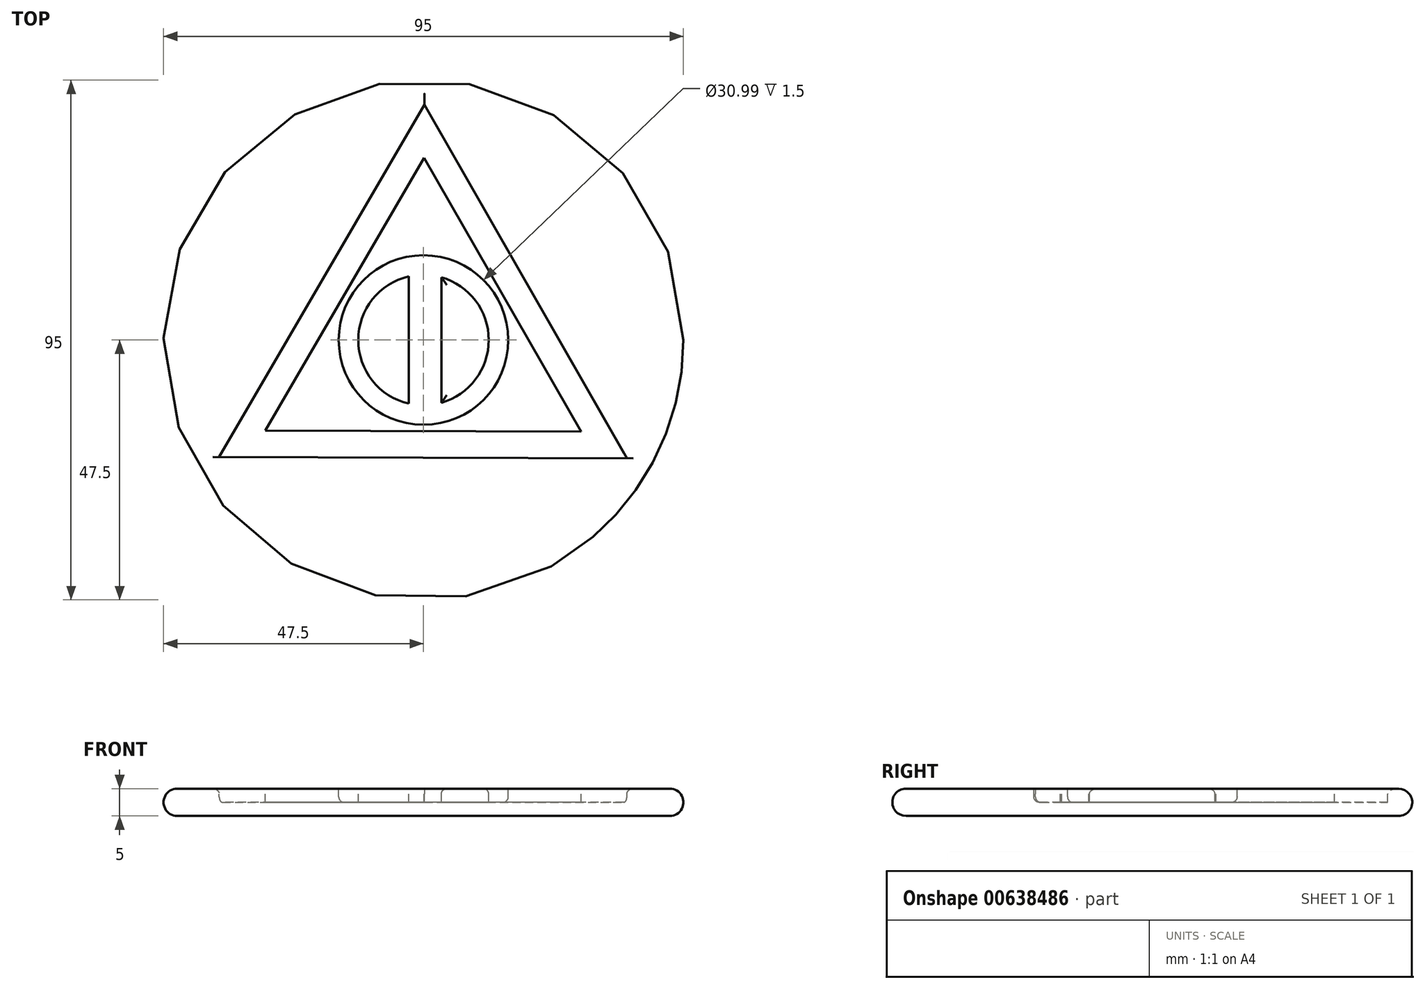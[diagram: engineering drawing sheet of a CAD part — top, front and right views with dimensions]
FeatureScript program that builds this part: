
annotation { "Feature Type Name" : "Feature", "Feature Type Description" : "" }
export const myFeature = defineFeature(function(context is Context, id is Id, definition is map)
    precondition{}
    {
        {
            var Q0;
            Q0=qCreatedBy(makeId("Top.planeOp"),FACE);
            var sketch = newSketch(context, id + "F0", { "sketchPlane" : qUnion([Q0])});
            skCircle(sketch, "E0", {"center": v(0, 0) * mm, "radius": 47.5 * mm});
            skSolve(sketch);
        }
        {
            var Q0;
            Q0=makeQuery(id+"F0.imprint","IMPRINT",FACE,{"disambiguationData":[TD([[makeQuery(id+"F0.imprint","IMPRINT",EDGE,{"derivedFrom":sQuery(id+"F0.wireOp",EDGE,"E0")}),1.0]])]});
            extrude(context, id + "F1", {"entities" : qUnion([Q0]), "depth" : 5 * mm, "offsetDistance" : 25.4 * mm});
        }
        {
            var Q0;
            Q0=makeQuery(id+"F1.opExtrude","CAP_FACE",FACE,{"disambiguationData":[OSD([sQuery(id+"F0.wireOp",EDGE,"E0")])],"isStart":false});
            var sketch = newSketch(context, id + "F2", { "sketchPlane" : qUnion([Q0])});
            skCircle(sketch, "E1.cCircle", {"center": v(0, 0) * mm, "radius": 21.5 * mm, "construction": true});
            skLineSegment(sketch, "E1.0", {"start": v(37.17, -21.65) * mm, "end": v(-37.34, -21.36) * mm});
            skLineSegment(sketch, "E1.1", {"start": v(-37.34, -21.36) * mm, "end": v(0.17, 43.01) * mm});
            skLineSegment(sketch, "E1.2", {"start": v(0.17, 43.01) * mm, "end": v(37.17, -21.65) * mm});
            skPoint(sketch, "E1.0.midPoint", {"position": v(-0.08, -21.5) * mm});
            skCircle(sketch, "E2.cCircle", {"center": v(0, 0) * mm, "radius": 16.66 * mm, "construction": true});
            skLineSegment(sketch, "E2.0", {"start": v(0.13, 33.32) * mm, "end": v(28.8, -16.77) * mm});
            skLineSegment(sketch, "E2.1", {"start": v(28.8, -16.77) * mm, "end": v(-28.92, -16.55) * mm});
            skLineSegment(sketch, "E2.2", {"start": v(-28.92, -16.55) * mm, "end": v(0.13, 33.32) * mm});
            skPoint(sketch, "E2.0.midPoint", {"position": v(14.46, 8.27) * mm});
            skSolve(sketch);
        }
        {
            var Q0;
            Q0 = qSketchRegion(id + "F2", true);
            extrude(context, id + "F3", {"entities" : qUnion([Q0]), "operationType" : NewBodyOperationType.REMOVE, "oppositeDirection" : true, "depth" : 2.5 * mm, "offsetDistance" : 25 * mm});
        }
        {
            var Q0;
            Q0=makeQuery(id+"F3.boolean.opBoolean","SPLIT",FACE,{"disambiguationData":[TD([makeQuery(id+"F3.opExtrude","SWEPT_FACE",FACE,{"disambiguationData":[OSD([sQuery(id+"F2.wireOp",EDGE,"E2.0")])]})])],"derivedFrom":makeQuery(id+"F1.opExtrude","CAP_FACE",FACE,{"disambiguationData":[OSD([sQuery(id+"F0.wireOp",EDGE,"E0")])],"isStart":false})});
            var sketch = newSketch(context, id + "F4", { "sketchPlane" : qUnion([Q0])});
            skCircle(sketch, "E3", {"center": v(0, 0) * mm, "radius": 15.5 * mm});
            skCircle(sketch, "E4", {"center": v(0, 0) * mm, "radius": 11.92 * mm});
            skSolve(sketch);
        }
        {
            var Q0;
            Q0=makeQuery(id+"F4.imprint","IMPRINT",FACE,{"disambiguationData":[TD([[makeQuery(id+"F4.imprint","IMPRINT",EDGE,{"derivedFrom":sQuery(id+"F4.wireOp",EDGE,"E3")}),1.0]])]});
            extrude(context, id + "F5", {"entities" : qUnion([Q0]), "operationType" : NewBodyOperationType.REMOVE, "oppositeDirection" : true, "depth" : 2.5 * mm, "offsetDistance" : 25 * mm});
        }
        {
            var Q0;
            {var subQ0=makeQuery(id+"F3.opExtrude","SWEPT_FACE",FACE,{"disambiguationData":[OSD([sQuery(id+"F2.wireOp",EDGE,"E2.0")])]});Q0=makeQuery(id+"F5.boolean.opBoolean","SPLIT",FACE,{"disambiguationData":[TD([makeQuery(id+"F3.boolean.opBoolean","COPY",FACE,{"derivedFrom":subQ0})])],"derivedFrom":makeQuery(id+"F3.boolean.opBoolean","SPLIT",FACE,{"disambiguationData":[TD([subQ0])],"derivedFrom":makeQuery(id+"F1.opExtrude","CAP_FACE",FACE,{"disambiguationData":[OSD([sQuery(id+"F0.wireOp",EDGE,"E0")])],"isStart":false})})});}
            var sketch = newSketch(context, id + "F6", { "sketchPlane" : qUnion([Q0])});
            skLineSegment(sketch, "E5.bottom", {"start": v(-2.7, 33.32) * mm, "end": v(3.26, 33.32) * mm});
            skLineSegment(sketch, "E5.top", {"start": v(-2.7, -16.67) * mm, "end": v(3.26, -16.67) * mm});
            skLineSegment(sketch, "E5.left", {"start": v(-2.7, 33.32) * mm, "end": v(-2.7, -16.67) * mm});
            skLineSegment(sketch, "E5.right", {"start": v(3.26, 33.32) * mm, "end": v(3.26, -16.67) * mm});
            skSolve(sketch);
        }
        {
            var Q0;
            {var subQ0=makeQuery(id+"F3.boolean.opBoolean","COPY",EDGE,{"derivedFrom":makeQuery(id+"F3.opExtrude","CAP_EDGE",EDGE,{"disambiguationData":[OSD([sQuery(id+"F2.wireOp",EDGE,"E2.2")])],"isStart":true})});var subQ3=sQuery(id+"F6.wireOp",EDGE,"E5.left");var subQ4=makeQuery(id+"F6.imprint","INTERSECT",VERTEX,{"derivedFrom":[subQ0,subQ3]});Q0=makeQuery(id+"F6.imprint","IMPRINT",FACE,{"disambiguationData":[TD([[makeQuery(id+"F6.imprint","IMPRINT",EDGE,{"disambiguationData":[TD([[subQ4,-1.0]])],"derivedFrom":subQ3}),1.0]])]});}
            var Q1;
            {var subQ0=sQuery(id+"F6.wireOp",EDGE,"E5.left");var subQ1=makeQuery(id+"F5.boolean.opBoolean","COPY",EDGE,{"derivedFrom":makeQuery(id+"F5.opExtrude","CAP_EDGE",EDGE,{"disambiguationData":[OSD([sQuery(id+"F4.wireOp",EDGE,"E3")])],"isStart":true})});var subQ2=makeQuery(id+"F6.imprint","INTERSECT",VERTEX,{"disambiguationData":[OD(0.0)],"derivedFrom":[subQ1,subQ0]});Q1=makeQuery(id+"F6.imprint","IMPRINT",FACE,{"disambiguationData":[TD([[makeQuery(id+"F6.imprint","IMPRINT",EDGE,{"disambiguationData":[TD([[subQ2,-1.0]])],"derivedFrom":subQ0}),1.0]])]});}
            var Q2;
            {var subQ0=sQuery(id+"F6.wireOp",EDGE,"E5.left");var subQ1=makeQuery(id+"F3.boolean.opBoolean","COPY",EDGE,{"derivedFrom":makeQuery(id+"F3.opExtrude","CAP_EDGE",EDGE,{"disambiguationData":[OSD([sQuery(id+"F2.wireOp",EDGE,"E2.1")])],"isStart":true})});var subQ2=makeQuery(id+"F6.imprint","INTERSECT",VERTEX,{"derivedFrom":[subQ1,subQ0]});Q2=makeQuery(id+"F6.imprint","IMPRINT",FACE,{"disambiguationData":[TD([[makeQuery(id+"F6.imprint","IMPRINT",EDGE,{"disambiguationData":[TD([[subQ2,1.0]])],"derivedFrom":subQ0}),1.0]])]});}
            extrude(context, id + "F7", {"entities" : qUnion([Q0, Q1, Q2]), "operationType" : NewBodyOperationType.REMOVE, "oppositeDirection" : true, "depth" : 2.5 * mm, "offsetDistance" : 25 * mm});
        }
        {
            var Q0;
            Q0=makeQuery(id+"F1.opExtrude","CAP_EDGE",EDGE,{"disambiguationData":[OSD([sQuery(id+"F0.wireOp",EDGE,"E0")])],"isStart":false});
            var Q1;
            Q1=makeQuery(id+"F1.opExtrude","CAP_FACE",FACE,{"disambiguationData":[OSD([sQuery(id+"F0.wireOp",EDGE,"E0")])],"isStart":true});
            fillet(context, id + "F8", {"entities" : qUnion([Q0, Q1]), "radius" : 2.5 * mm, "tangentPropagation" : true, "allowEdgeOverflow" : false});
        }
        {
            var Q0;
            {var subQ0=sQuery(id+"F4.wireOp",EDGE,"E4");Q0=makeQuery(id+"F7.boolean.opBoolean","SPLIT",EDGE,{"disambiguationData":[TD([makeQuery(id+"F7.opExtrude","SWEPT_FACE",FACE,{"disambiguationData":[OSD([sQuery(id+"F6.wireOp",EDGE,"E5.right")])]})])],"derivedFrom":makeQuery(id+"F5.boolean.opBoolean","COPY",EDGE,{"derivedFrom":makeQuery(id+"F5.opExtrude","CAP_EDGE",EDGE,{"disambiguationData":[OSD([subQ0])],"isStart":true})})});}
            var Q1;
            {var subQ0=sQuery(id+"F6.wireOp",EDGE,"E5.right");Q1=makeQuery(id+"F7.boolean.opBoolean","COPY",EDGE,{"disambiguationData":[TD([makeQuery(id+"F5.boolean.opBoolean","COPY",FACE,{"derivedFrom":makeQuery(id+"F5.opExtrude","SWEPT_FACE",FACE,{"disambiguationData":[OSD([sQuery(id+"F4.wireOp",EDGE,"E4")])]})})])],"derivedFrom":makeQuery(id+"F7.opExtrude","CAP_EDGE",EDGE,{"disambiguationData":[OSD([subQ0])],"isStart":true})});}
            var Q2;
            {var subQ0=sQuery(id+"F6.wireOp",EDGE,"E5.left");Q2=makeQuery(id+"F7.boolean.opBoolean","COPY",EDGE,{"disambiguationData":[TD([makeQuery(id+"F5.boolean.opBoolean","COPY",FACE,{"derivedFrom":makeQuery(id+"F5.opExtrude","SWEPT_FACE",FACE,{"disambiguationData":[OSD([sQuery(id+"F4.wireOp",EDGE,"E4")])]})})])],"derivedFrom":makeQuery(id+"F7.opExtrude","CAP_EDGE",EDGE,{"disambiguationData":[OSD([subQ0])],"isStart":true})});}
            var Q3;
            {var subQ0=sQuery(id+"F6.wireOp",EDGE,"E5.left");var subQ1=sQuery(id+"F4.wireOp",EDGE,"E3");Q3=makeQuery(id+"F7.boolean.opBoolean","SPLIT",EDGE,{"disambiguationData":[TD([makeQuery(id+"F7.opExtrude","SWEPT_FACE",FACE,{"disambiguationData":[OSD([subQ0])]})])],"derivedFrom":makeQuery(id+"F5.boolean.opBoolean","COPY",EDGE,{"derivedFrom":makeQuery(id+"F5.opExtrude","CAP_EDGE",EDGE,{"disambiguationData":[OSD([subQ1])],"isStart":false})})});}
            var Q4;
            {var subQ0=sQuery(id+"F4.wireOp",EDGE,"E3");Q4=makeQuery(id+"F7.boolean.opBoolean","SPLIT",EDGE,{"disambiguationData":[TD([makeQuery(id+"F7.opExtrude","SWEPT_FACE",FACE,{"disambiguationData":[OSD([sQuery(id+"F6.wireOp",EDGE,"E5.right")])]})])],"derivedFrom":makeQuery(id+"F5.boolean.opBoolean","COPY",EDGE,{"derivedFrom":makeQuery(id+"F5.opExtrude","CAP_EDGE",EDGE,{"disambiguationData":[OSD([subQ0])],"isStart":true})})});}
            var Q5;
            {var subQ0=sQuery(id+"F6.wireOp",EDGE,"E5.right");Q5=makeQuery(id+"F7.boolean.opBoolean","COPY",EDGE,{"disambiguationData":[TD([makeQuery(id+"F3.boolean.opBoolean","COPY",FACE,{"derivedFrom":makeQuery(id+"F3.opExtrude","SWEPT_FACE",FACE,{"disambiguationData":[OSD([sQuery(id+"F2.wireOp",EDGE,"E2.0")])]})})])],"derivedFrom":makeQuery(id+"F7.opExtrude","CAP_EDGE",EDGE,{"disambiguationData":[OSD([subQ0])],"isStart":true})});}
            var Q6;
            {var subQ0=sQuery(id+"F6.wireOp",EDGE,"E5.left");Q6=makeQuery(id+"F7.boolean.opBoolean","COPY",EDGE,{"disambiguationData":[TD([makeQuery(id+"F3.boolean.opBoolean","COPY",FACE,{"derivedFrom":makeQuery(id+"F3.opExtrude","SWEPT_FACE",FACE,{"disambiguationData":[OSD([sQuery(id+"F2.wireOp",EDGE,"E2.2")])]})})])],"derivedFrom":makeQuery(id+"F7.opExtrude","CAP_EDGE",EDGE,{"disambiguationData":[OSD([subQ0])],"isStart":true})});}
            var Q7;
            {var subQ0=sQuery(id+"F2.wireOp",EDGE,"E2.1");Q7=makeQuery(id+"F7.boolean.opBoolean","SPLIT",EDGE,{"disambiguationData":[TD([makeQuery(id+"F3.boolean.opBoolean","COPY",FACE,{"derivedFrom":makeQuery(id+"F3.opExtrude","SWEPT_FACE",FACE,{"disambiguationData":[OSD([sQuery(id+"F2.wireOp",EDGE,"E2.2")])]})})])],"derivedFrom":makeQuery(id+"F3.boolean.opBoolean","COPY",EDGE,{"derivedFrom":makeQuery(id+"F3.opExtrude","CAP_EDGE",EDGE,{"disambiguationData":[OSD([subQ0])],"isStart":true})})});}
            var Q8;
            {var subQ0=sQuery(id+"F2.wireOp",EDGE,"E2.1");Q8=makeQuery(id+"F7.boolean.opBoolean","SPLIT",EDGE,{"disambiguationData":[TD([makeQuery(id+"F3.boolean.opBoolean","COPY",FACE,{"derivedFrom":makeQuery(id+"F3.opExtrude","SWEPT_FACE",FACE,{"disambiguationData":[OSD([sQuery(id+"F2.wireOp",EDGE,"E2.0")])]})})])],"derivedFrom":makeQuery(id+"F3.boolean.opBoolean","COPY",EDGE,{"derivedFrom":makeQuery(id+"F3.opExtrude","CAP_EDGE",EDGE,{"disambiguationData":[OSD([subQ0])],"isStart":true})})});}
            var Q9;
            Q9=makeQuery(id+"F3.boolean.opBoolean","COPY",EDGE,{"derivedFrom":makeQuery(id+"F3.opExtrude","CAP_EDGE",EDGE,{"disambiguationData":[OSD([sQuery(id+"F2.wireOp",EDGE,"E2.0")])],"isStart":true})});
            var Q10;
            Q10=makeQuery(id+"F3.boolean.opBoolean","COPY",EDGE,{"derivedFrom":makeQuery(id+"F3.opExtrude","CAP_EDGE",EDGE,{"disambiguationData":[OSD([sQuery(id+"F2.wireOp",EDGE,"E2.2")])],"isStart":true})});
            var Q11;
            Q11=makeQuery(id+"F3.boolean.opBoolean","COPY",EDGE,{"derivedFrom":makeQuery(id+"F3.opExtrude","CAP_EDGE",EDGE,{"disambiguationData":[OSD([sQuery(id+"F2.wireOp",EDGE,"E1.1")])],"isStart":true})});
            var Q12;
            Q12=makeQuery(id+"F3.boolean.opBoolean","COPY",EDGE,{"derivedFrom":makeQuery(id+"F3.opExtrude","CAP_EDGE",EDGE,{"disambiguationData":[OSD([sQuery(id+"F2.wireOp",EDGE,"E1.2")])],"isStart":true})});
            var Q13;
            Q13=makeQuery(id+"F3.boolean.opBoolean","COPY",EDGE,{"derivedFrom":makeQuery(id+"F3.opExtrude","CAP_EDGE",EDGE,{"disambiguationData":[OSD([sQuery(id+"F2.wireOp",EDGE,"E1.0")])],"isStart":false})});
            fillet(context, id + "F9", {"entities" : qUnion([Q0, Q1, Q2, Q3, Q4, Q5, Q6, Q7, Q8, Q9, Q10, Q11, Q12, Q13]), "radius" : 1 * mm, "tangentPropagation" : true, "allowEdgeOverflow" : false});
        }
    });
